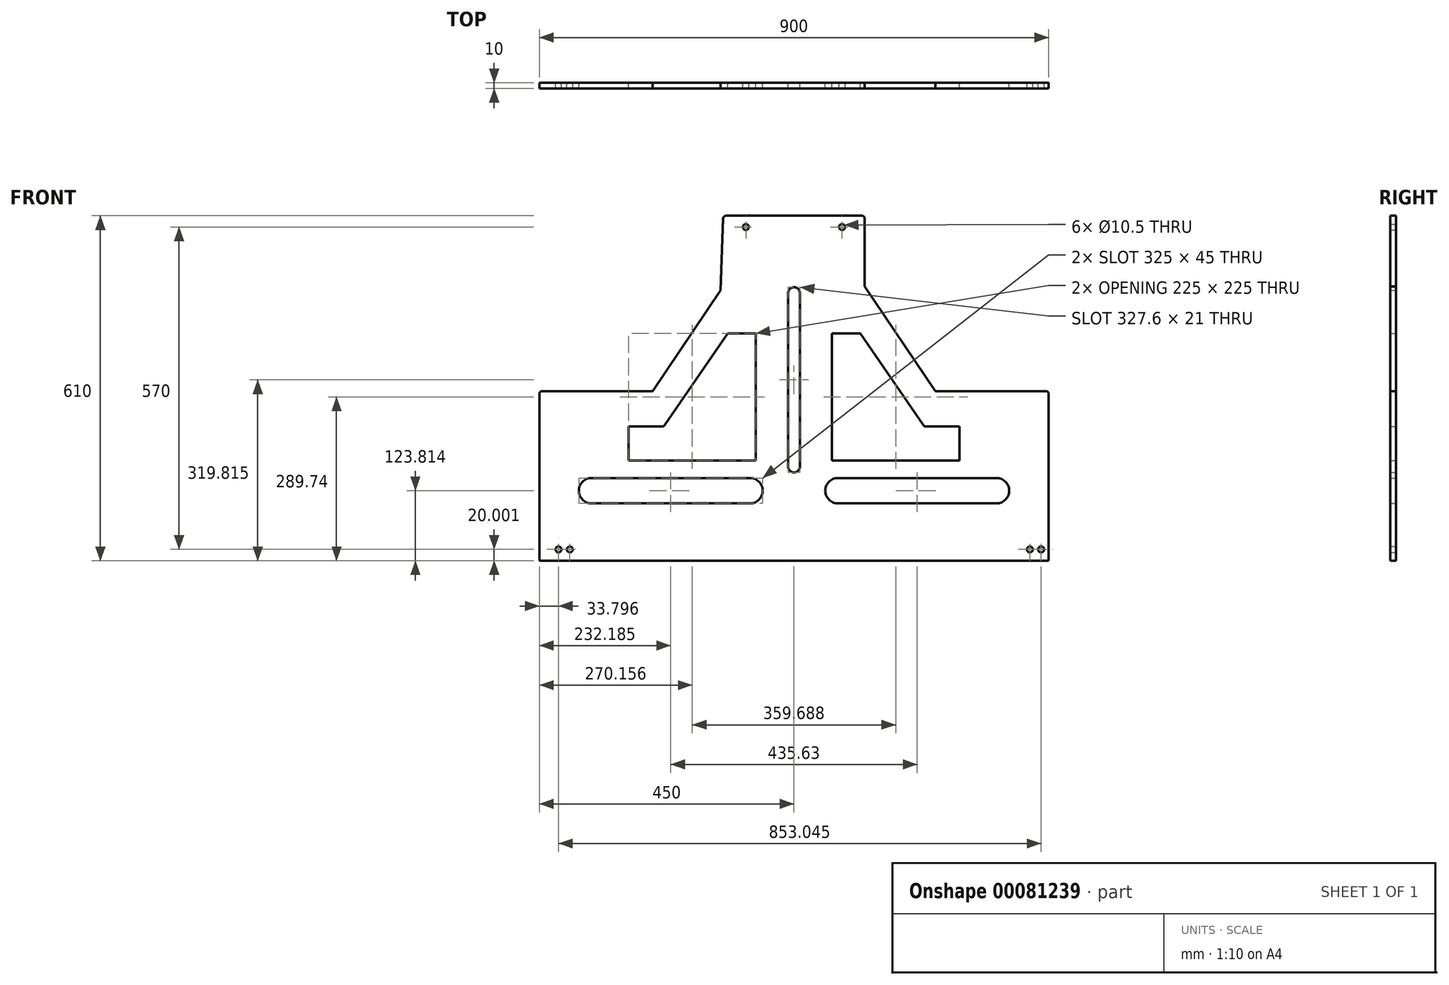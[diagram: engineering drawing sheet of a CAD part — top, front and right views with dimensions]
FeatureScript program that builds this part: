
annotation { "Feature Type Name" : "Feature", "Feature Type Description" : "" }
export const myFeature = defineFeature(function(context is Context, id is Id, definition is map)
    precondition{}
    {
        {
            var Q0;
            Q0=qCreatedBy(makeId("Front.planeOp"),FACE);
            var sketch = newSketch(context, id + "F0", { "sketchPlane" : qUnion([Q0])});
            skLineSegment(sketch, "E0", {"start": v(-450, 62.76) * mm, "end": v(-450, -237.24) * mm});
            skLineSegment(sketch, "E1", {"start": v(-450, -237.24) * mm, "end": v(0, -237.24) * mm});
            skLineSegment(sketch, "E2", {"start": v(-450, 62.76) * mm, "end": v(-250, 62.76) * mm});
            skLineSegment(sketch, "E3", {"start": v(-250, 62.76) * mm, "end": v(-129.6, 240.96) * mm});
            skLineSegment(sketch, "E4.MirrorCS", {"start": v(450, 62.76) * mm, "end": v(250, 62.76) * mm});
            skLineSegment(sketch, "E5.MirrorCS", {"start": v(450, 62.76) * mm, "end": v(450, -237.24) * mm});
            skLineSegment(sketch, "E6.MirrorCS", {"start": v(450, -237.24) * mm, "end": v(0, -237.24) * mm});
            skLineSegment(sketch, "E7.MirrorCS", {"start": v(250, 62.76) * mm, "end": v(125, 247.76) * mm});
            skLineSegment(sketch, "E8", {"start": v(125, 247.76) * mm, "end": v(125, 372.76) * mm});
            skLineSegment(sketch, "E9.MirrorCS", {"start": v(-129.6, 240.96) * mm, "end": v(-125, 372.76) * mm});
            skLineSegment(sketch, "E10", {"start": v(-125, 372.76) * mm, "end": v(125, 372.76) * mm});
            skPoint(sketch, "E11.orphan", {"position": v(0, 432.76) * mm});
            skCircle(sketch, "E12", {"center": v(85, 352.76) * mm, "radius": 5.25 * mm});
            skCircle(sketch, "E13", {"center": v(-85, 352.76) * mm, "radius": 5.25 * mm});
            skLineSegment(sketch, "E14", {"start": v(-77.82, -90.93) * mm, "end": v(-357.82, -90.93) * mm});
            skLineSegment(sketch, "E15", {"start": v(-77.82, -135.93) * mm, "end": v(-357.82, -135.93) * mm});
            skLineSegment(sketch, "E16.MirrorCS", {"start": v(77.82, -90.93) * mm, "end": v(357.82, -90.93) * mm});
            skLineSegment(sketch, "E17.MirrorCS", {"start": v(77.82, -135.93) * mm, "end": v(357.82, -135.93) * mm});
            skArc(sketch, "E18", {"start": v(357.82, -90.93) * mm, "mid": v(380.32, -113.43) * mm, "end": v(357.82, -135.93) * mm});
            skArc(sketch, "E19", {"start": v(77.82, -90.93) * mm, "mid": v(55.32, -113.43) * mm, "end": v(77.82, -135.93) * mm});
            skArc(sketch, "E20", {"start": v(-77.82, -90.93) * mm, "mid": v(-55.32, -113.43) * mm, "end": v(-77.82, -135.93) * mm});
            skLineSegment(sketch, "E21", {"start": v(-10.5, 235.9) * mm, "end": v(-10.5, 0) * mm});
            skArc(sketch, "E22", {"start": v(-357.82, -90.93) * mm, "mid": v(-380.32, -113.43) * mm, "end": v(-357.82, -135.93) * mm});
            skLineSegment(sketch, "E23.bottom", {"start": v(-292.34, 0) * mm, "end": v(-230.37, 0) * mm});
            skLineSegment(sketch, "E23.top", {"start": v(-292.34, -60) * mm, "end": v(-67.34, -60) * mm});
            skLineSegment(sketch, "E23.left", {"start": v(-292.34, 0) * mm, "end": v(-292.34, -60) * mm});
            skLineSegment(sketch, "E23.right", {"start": v(-67.34, 0) * mm, "end": v(-67.34, -60) * mm});
            skLineSegment(sketch, "E24", {"start": v(-67.34, 0) * mm, "end": v(-67.34, 165) * mm});
            skLineSegment(sketch, "E25", {"start": v(-67.34, 165) * mm, "end": v(-117.34, 165) * mm});
            skLineSegment(sketch, "E26", {"start": v(-117.34, 165) * mm, "end": v(-230.37, 0) * mm});
            skLineSegment(sketch, "E27.MirrorCS", {"start": v(67.34, 165) * mm, "end": v(117.34, 165) * mm});
            skLineSegment(sketch, "E28.MirrorCS", {"start": v(117.34, 165) * mm, "end": v(230.37, 0) * mm});
            skLineSegment(sketch, "E29.MirrorCS", {"start": v(292.34, 0) * mm, "end": v(230.37, 0) * mm});
            skLineSegment(sketch, "E30.MirrorCS", {"start": v(292.34, -60) * mm, "end": v(67.34, -60) * mm});
            skLineSegment(sketch, "E31.MirrorCS", {"start": v(67.34, 0) * mm, "end": v(67.34, 165) * mm});
            skLineSegment(sketch, "E32.MirrorCS", {"start": v(67.34, 0) * mm, "end": v(67.34, -60) * mm});
            skLineSegment(sketch, "E33.MirrorCS", {"start": v(292.34, 0) * mm, "end": v(292.34, -60) * mm});
            skCircle(sketch, "E34", {"center": v(-416.2, -217.24) * mm, "radius": 5.25 * mm});
            skCircle(sketch, "E35", {"center": v(416.84, -217.24) * mm, "radius": 5.25 * mm});
            skPoint(sketch, "E36.orphan", {"position": v(0, -202.88) * mm});
            skLineSegment(sketch, "E37.MirrorCS", {"start": v(10.5, 235.87) * mm, "end": v(10.5, 0.02) * mm});
            skLineSegment(sketch, "E38.MirrorCS", {"start": v(-10.5, 235.87) * mm, "end": v(-10.5, 235.9) * mm});
            skPoint(sketch, "E39.MirrorCS.end.orphan", {"position": v(-21, 63.33) * mm});
            skPoint(sketch, "E39.MirrorCS.start.orphan", {"position": v(-21, 372.76) * mm});
            skPoint(sketch, "E40.orphan", {"position": v(0, 372.76) * mm});
            skPoint(sketch, "E41.start.orphan", {"position": v(0, 235.9) * mm});
            skPoint(sketch, "E42.start.orphan", {"position": v(0, 63.33) * mm});
            skArc(sketch, "E43", {"start": v(-10.5, 235.87) * mm, "mid": v(0, 246.37) * mm, "end": v(10.5, 235.87) * mm});
            skLineSegment(sketch, "E44", {"start": v(10.5, 0.02) * mm, "end": v(10.5, -70.73) * mm});
            skLineSegment(sketch, "E45", {"start": v(-10.5, 0) * mm, "end": v(-10.5, -70.73) * mm});
            skPoint(sketch, "E45.endSnap0", {"position": v(-6.21, -70.73) * mm});
            skPoint(sketch, "E46.orphan", {"position": v(-22.92, -70.73) * mm});
            skArc(sketch, "E47", {"start": v(10.5, -70.73) * mm, "mid": v(0, -81.23) * mm, "end": v(-10.5, -70.73) * mm});
            skCircle(sketch, "E48", {"center": v(-396.2, -217.24) * mm, "radius": 5.25 * mm});
            skCircle(sketch, "E49", {"center": v(436.84, -217.24) * mm, "radius": 5.25 * mm});
            skLineSegment(sketch, "E50", {"start": v(-85, 352.76) * mm, "end": v(85, 352.76) * mm, "construction": true});
            skLineSegment(sketch, "E51", {"start": v(-85, 352.76) * mm, "end": v(-125.7, 352.76) * mm, "construction": true});
            skLineSegment(sketch, "E52", {"start": v(85, 352.76) * mm, "end": v(125, 352.76) * mm, "construction": true});
            skLineSegment(sketch, "E53", {"start": v(-85, 352.76) * mm, "end": v(-85, 372.76) * mm, "construction": true});
            skLineSegment(sketch, "E54", {"start": v(-10.5, 117.95) * mm, "end": v(10.5, 117.95) * mm, "construction": true});
            skSolve(sketch);
        }
        {
            var Q0;
            Q0=makeQuery(id+"F0.imprint","IMPRINT",FACE,{"disambiguationData":[TD([[makeQuery(id+"F0.imprint","IMPRINT",EDGE,{"derivedFrom":sQuery(id+"F0.wireOp",EDGE,"E0")}),1.0]])]});
            extrude(context, id + "F1", {"entities" : qUnion([Q0]), "depth" : 10 * mm});
        }
        {
            var Q0;
            Q0=makeQuery(id+"F1.opExtrude","SWEPT_EDGE",EDGE,{"disambiguationData":[OSD([sQuery(id+"F0.wireOp",EDGE,"E23.bottom"),sQuery(id+"F0.wireOp",EDGE,"E26")])]});
            var Q1;
            Q1=makeQuery(id+"F1.opExtrude","SWEPT_EDGE",EDGE,{"disambiguationData":[OSD([sQuery(id+"F0.wireOp",EDGE,"E28.MirrorCS"),sQuery(id+"F0.wireOp",EDGE,"E29.MirrorCS")])]});
            fillet(context, id + "F2", {"entities" : qUnion([Q0, Q1]), "radius" : 5 * mm, "tangentPropagation" : true, "allowEdgeOverflow" : false});
        }
        {
            var Q0;
            Q0=makeQuery(id+"F1.opExtrude","SWEPT_EDGE",EDGE,{"disambiguationData":[OSD([sQuery(id+"F0.wireOp",EDGE,"E0"),sQuery(id+"F0.wireOp",EDGE,"E2")])]});
            var Q1;
            Q1=makeQuery(id+"F1.opExtrude","SWEPT_EDGE",EDGE,{"disambiguationData":[OSD([sQuery(id+"F0.wireOp",EDGE,"E9.MirrorCS"),sQuery(id+"F0.wireOp",EDGE,"E10")])]});
            var Q2;
            Q2=makeQuery(id+"F1.opExtrude","SWEPT_EDGE",EDGE,{"disambiguationData":[OSD([sQuery(id+"F0.wireOp",EDGE,"E8"),sQuery(id+"F0.wireOp",EDGE,"E10")])]});
            var Q3;
            Q3=makeQuery(id+"F1.opExtrude","SWEPT_EDGE",EDGE,{"disambiguationData":[OSD([sQuery(id+"F0.wireOp",EDGE,"E4.MirrorCS"),sQuery(id+"F0.wireOp",EDGE,"E5.MirrorCS")])]});
            fillet(context, id + "F3", {"entities" : qUnion([Q0, Q1, Q2, Q3]), "radius" : 5 * mm, "tangentPropagation" : true, "allowEdgeOverflow" : false});
        }
    });
